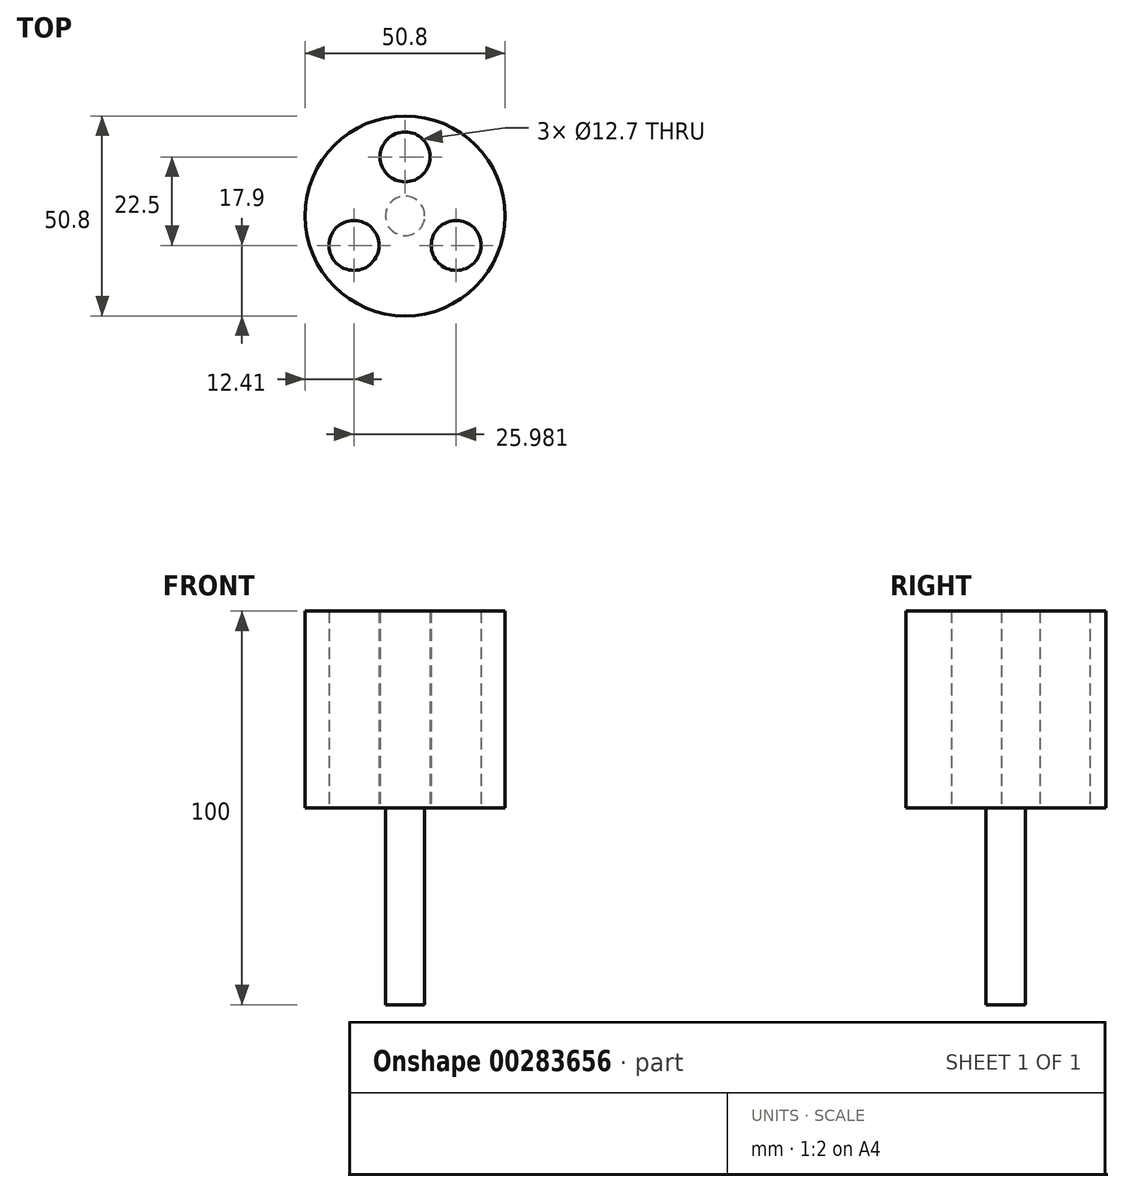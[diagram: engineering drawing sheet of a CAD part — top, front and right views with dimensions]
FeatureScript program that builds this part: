
annotation { "Feature Type Name" : "Feature", "Feature Type Description" : "" }
export const myFeature = defineFeature(function(context is Context, id is Id, definition is map)
    precondition{}
    {
        {
            var Q0;
            Q0=qCreatedBy(makeId("Top.planeOp"),FACE);
            var sketch = newSketch(context, id + "F0", { "sketchPlane" : qUnion([Q0])});
            skCircle(sketch, "E0", {"center": v(0, 0) * mm, "radius": 25.4 * mm});
            skCircle(sketch, "E1", {"center": v(0, 15) * mm, "radius": 6.35 * mm});
            skCircle(sketch, "E2.1.0", {"center": v(-13, -7.5) * mm, "radius": 6.35 * mm});
            skCircle(sketch, "E2.2.0", {"center": v(13, -7.5) * mm, "radius": 6.35 * mm});
            skSolve(sketch);
        }
        {
            var Q0;
            Q0=makeQuery(id+"F0.imprint","IMPRINT",FACE,{"disambiguationData":[TD([[makeQuery(id+"F0.imprint","IMPRINT",EDGE,{"derivedFrom":sQuery(id+"F0.wireOp",EDGE,"E0")}),1.0]])]});
            extrude(context, id + "F1", {"entities" : qUnion([Q0]), "endBound" : BoundingType.SYMMETRIC, "depth" : 50 * mm});
        }
        {
            var Q0;
            Q0=makeQuery(id+"F1.opExtrude","CAP_FACE",FACE,{"disambiguationData":[OSD([sQuery(id+"F0.wireOp",EDGE,"E0"),sQuery(id+"F0.wireOp",EDGE,"E1"),sQuery(id+"F0.wireOp",EDGE,"E2.1.0"),sQuery(id+"F0.wireOp",EDGE,"E2.2.0")])],"isStart":true});
            var sketch = newSketch(context, id + "F2", { "sketchPlane" : qUnion([Q0])});
            skCircle(sketch, "E3", {"center": v(0, 0) * mm, "radius": 5 * mm});
            skSolve(sketch);
        }
        {
            var Q0;
            Q0=makeQuery(id+"F2.imprint","IMPRINT",FACE,{"disambiguationData":[TD([[makeQuery(id+"F2.imprint","IMPRINT",EDGE,{"derivedFrom":sQuery(id+"F2.wireOp",EDGE,"E3")}),1.0]])]});
            extrude(context, id + "F3", {"entities" : qUnion([Q0]), "operationType" : NewBodyOperationType.ADD, "depth" : 50 * mm});
        }
    });
